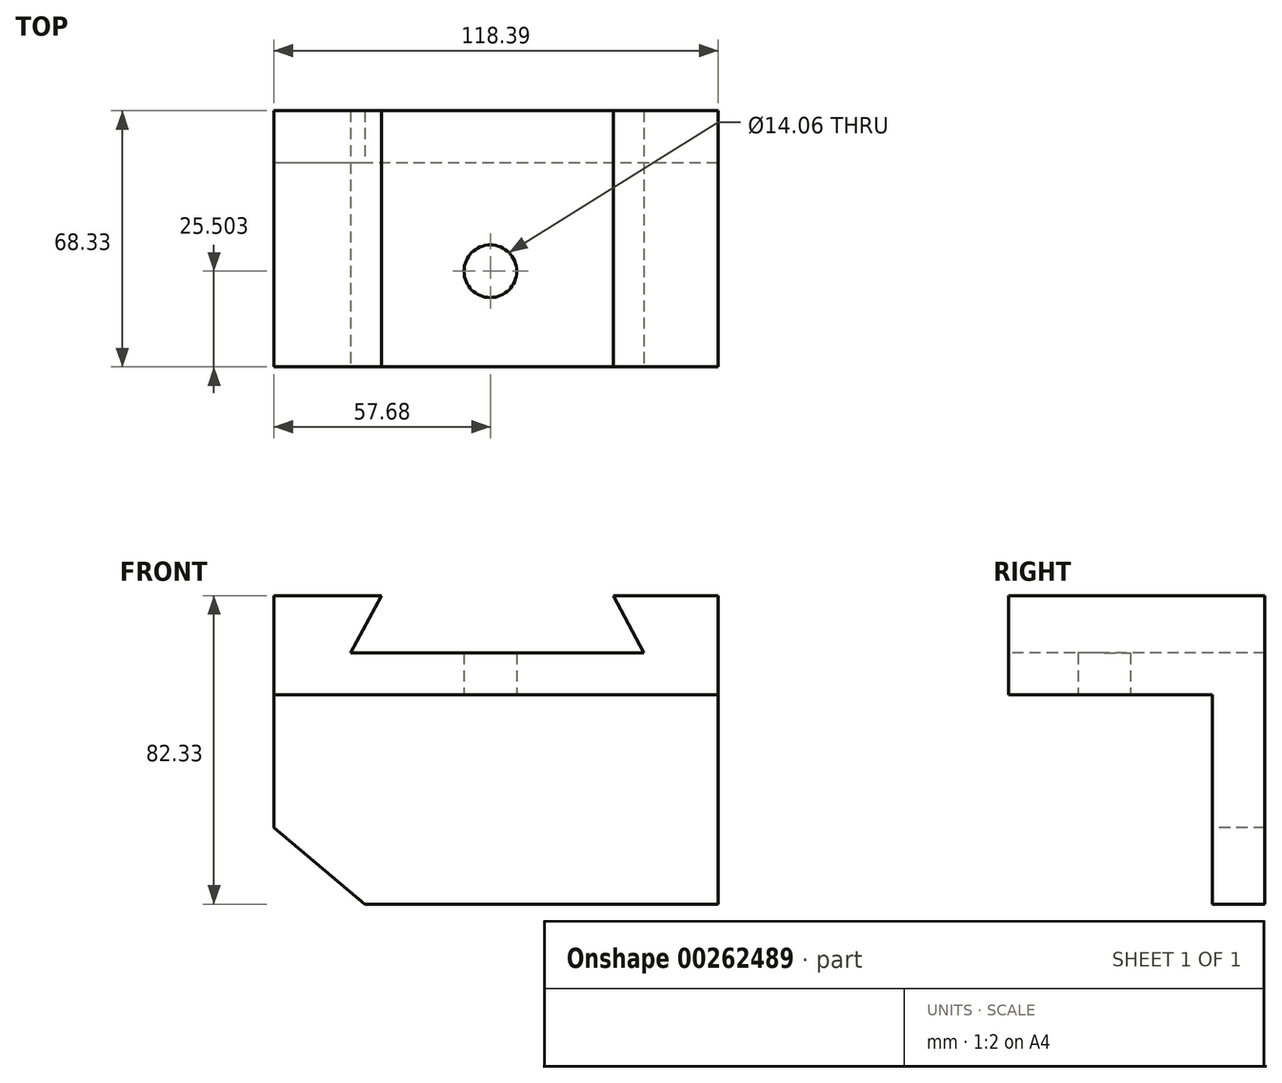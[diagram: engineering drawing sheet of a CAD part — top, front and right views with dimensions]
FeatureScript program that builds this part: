
annotation { "Feature Type Name" : "Feature", "Feature Type Description" : "" }
export const myFeature = defineFeature(function(context is Context, id is Id, definition is map)
    precondition{}
    {
        {
            var Q0;
            Q0=qCreatedBy(makeId("Front.planeOp"),FACE);
            var sketch = newSketch(context, id + "F0", { "sketchPlane" : qUnion([Q0])});
            skLineSegment(sketch, "E0.bottom", {"start": v(-57.68, 43.5) * mm, "end": v(60.7, 43.5) * mm});
            skLineSegment(sketch, "E0.top", {"start": v(-57.68, -38.84) * mm, "end": v(60.7, -38.84) * mm});
            skLineSegment(sketch, "E0.left", {"start": v(-57.68, 43.5) * mm, "end": v(-57.68, -38.84) * mm});
            skLineSegment(sketch, "E0.right", {"start": v(60.7, 43.5) * mm, "end": v(60.7, -38.84) * mm});
            skSolve(sketch);
        }
        {
            var Q0;
            Q0 = qSketchRegion(id + "F0", true);
            extrude(context, id + "F1", {"entities" : qUnion([Q0]), "depth" : 68.33 * mm});
        }
        {
            var Q0;
            Q0=makeQuery(id+"F1.opExtrude","SWEPT_FACE",FACE,{"disambiguationData":[OSD([sQuery(id+"F0.wireOp",EDGE,"E0.top")])]});
            var sketch = newSketch(context, id + "F2", { "sketchPlane" : qUnion([Q0])});
            skLineSegment(sketch, "E1", {"start": v(60.7, 13.96) * mm, "end": v(-57.68, 13.96) * mm});
            skSolve(sketch);
        }
        {
            var Q0;
            {var subQ0=sQuery(id+"F2.wireOp",EDGE,"E1");Q0=makeQuery(id+"F2.imprint","IMPRINT",FACE,{"disambiguationData":[TD([[makeQuery(id+"F2.imprint","IMPRINT",EDGE,{"derivedFrom":subQ0}),-1.0]])]});}
            extrude(context, id + "F3", {"entities" : qUnion([Q0]), "operationType" : NewBodyOperationType.REMOVE, "oppositeDirection" : true, "depth" : 55.88 * mm});
        }
        {
            var Q0;
            Q0=makeQuery(id+"F3.boolean.opBoolean","COPY",FACE,{"derivedFrom":makeQuery(id+"F3.opExtrude","SWEPT_FACE",FACE,{"disambiguationData":[OSD([sQuery(id+"F2.wireOp",EDGE,"E1")])]})});
            var sketch = newSketch(context, id + "F4", { "sketchPlane" : qUnion([Q0])});
            skLineSegment(sketch, "E2", {"start": v(35.59, -38.84) * mm, "end": v(60.7, -19.54) * mm});
            skLineSegment(sketch, "E3", {"start": v(60.7, -19.54) * mm, "end": v(35.59, -38.84) * mm});
            skLineSegment(sketch, "E4", {"start": v(-33.5, -38.84) * mm, "end": v(-57.68, -18.37) * mm});
            skSolve(sketch);
        }
        {
            var Q0;
            {var subQ0=sQuery(id+"F4.wireOp",EDGE,"E3");Q0=makeQuery(id+"F4.imprint","IMPRINT",FACE,{"disambiguationData":[TD([[makeQuery(id+"F4.imprint","IMPRINT",EDGE,{"derivedFrom":subQ0}),1.0]])]});}
            var Q1;
            {var subQ0=sQuery(id+"F4.wireOp",EDGE,"E4");Q1=makeQuery(id+"F4.imprint","IMPRINT",FACE,{"disambiguationData":[TD([[makeQuery(id+"F4.imprint","IMPRINT",EDGE,{"derivedFrom":subQ0}),1.0]])]});}
            extrude(context, id + "F5", {"entities" : qUnion([Q0, Q1]), "operationType" : NewBodyOperationType.REMOVE, "oppositeDirection" : true, "depth" : 25.4 * mm});
        }
        {
            var Q0;
            Q0=makeQuery(id+"F1.opExtrude","CAP_FACE",FACE,{"disambiguationData":[OSD([sQuery(id+"F0.wireOp",EDGE,"E0.bottom"),sQuery(id+"F0.wireOp",EDGE,"E0.top"),sQuery(id+"F0.wireOp",EDGE,"E0.left"),sQuery(id+"F0.wireOp",EDGE,"E0.right")])],"isStart":false});
            var sketch = newSketch(context, id + "F6", { "sketchPlane" : qUnion([Q0])});
            skLineSegment(sketch, "E5", {"start": v(32.8, 43.5) * mm, "end": v(40.94, 28.14) * mm});
            skLineSegment(sketch, "E6", {"start": v(40.94, 28.14) * mm, "end": v(-37.21, 28.14) * mm});
            skLineSegment(sketch, "E7", {"start": v(-37.21, 28.14) * mm, "end": v(-29.07, 43.5) * mm});
            skSolve(sketch);
        }
        {
            var Q0;
            {var subQ0=sQuery(id+"F6.wireOp",EDGE,"E5");Q0=makeQuery(id+"F6.imprint","IMPRINT",FACE,{"disambiguationData":[TD([[makeQuery(id+"F6.imprint","IMPRINT",EDGE,{"derivedFrom":subQ0}),-1.0]])]});}
            extrude(context, id + "F7", {"entities" : qUnion([Q0]), "operationType" : NewBodyOperationType.REMOVE, "oppositeDirection" : true, "depth" : 87.12 * mm});
        }
        {
            var Q0;
            Q0=makeQuery(id+"F3.boolean.opBoolean","COPY",FACE,{"derivedFrom":makeQuery(id+"F3.opExtrude","CAP_FACE",FACE,{"disambiguationData":[OSD([sQuery(id+"F0.wireOp",EDGE,"E0.top"),sQuery(id+"F0.wireOp",EDGE,"E0.left"),sQuery(id+"F0.wireOp",EDGE,"E0.right"),sQuery(id+"F2.wireOp",EDGE,"E1")])],"isStart":false})});
            var sketch = newSketch(context, id + "F8", { "sketchPlane" : qUnion([Q0])});
            skCircle(sketch, "E8", {"center": v(0, 42.83) * mm, "radius": 7.03 * mm});
            skSolve(sketch);
        }
        {
            var Q0;
            Q0 = qSketchRegion(id + "F8", true);
            extrude(context, id + "F9", {"entities" : qUnion([Q0]), "operationType" : NewBodyOperationType.REMOVE, "oppositeDirection" : true, "depth" : 25.4 * mm});
        }
    });
